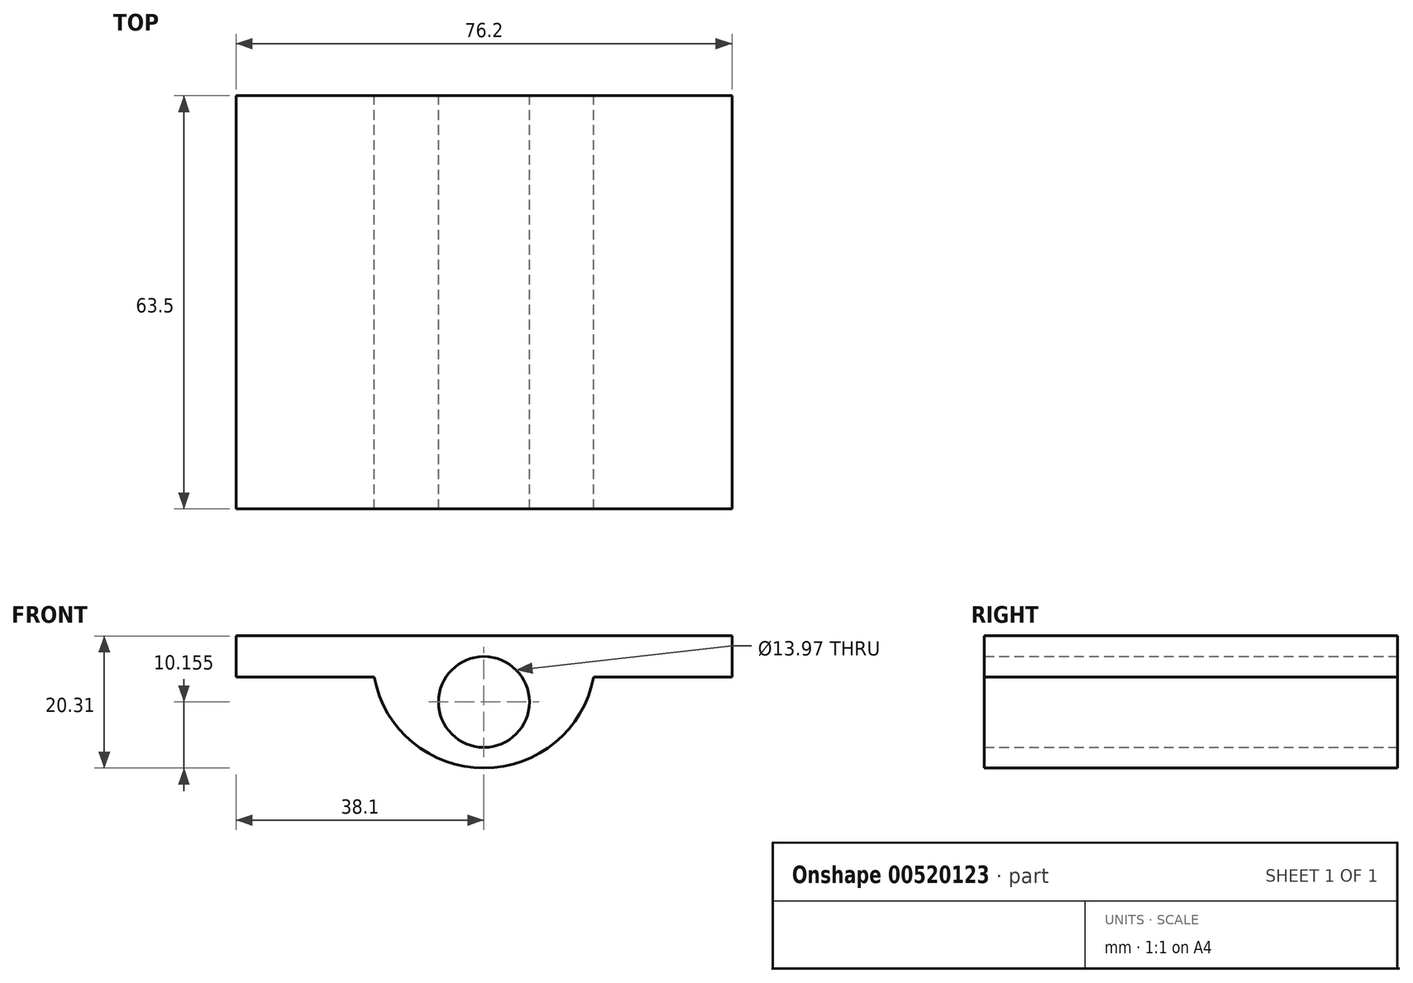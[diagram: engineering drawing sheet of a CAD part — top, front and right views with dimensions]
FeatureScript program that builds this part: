
annotation { "Feature Type Name" : "Feature", "Feature Type Description" : "" }
export const myFeature = defineFeature(function(context is Context, id is Id, definition is map)
    precondition{}
    {
        {
            var Q0;
            Q0=qCreatedBy(makeId("Front.planeOp"),FACE);
            var sketch = newSketch(context, id + "F0", { "sketchPlane" : qUnion([Q0])});
            skLineSegment(sketch, "E0.MirrorCS", {"start": v(38.1, 3.17) * mm, "end": v(38.1, -3.17) * mm});
            skLineSegment(sketch, "E1.MirrorCS", {"start": v(-38.1, 3.17) * mm, "end": v(-38.1, -3.17) * mm});
            skLineSegment(sketch, "E2.MirrorCS", {"start": v(38.1, -3.17) * mm, "end": v(16.85, -3.17) * mm});
            skLineSegment(sketch, "E3.MirrorCS", {"start": v(-38.1, -3.17) * mm, "end": v(-16.85, -3.17) * mm});
            skArc(sketch, "E4.MirrorCS", {"start": v(-16.85, -3.17) * mm, "mid": v(0, -17.14) * mm, "end": v(16.85, -3.18) * mm});
            skCircle(sketch, "E5", {"center": v(0, -6.99) * mm, "radius": 6.99 * mm});
            skLineSegment(sketch, "E6", {"start": v(0, 3.17) * mm, "end": v(38.1, 3.17) * mm});
            skLineSegment(sketch, "E7", {"start": v(0, 3.17) * mm, "end": v(-38.1, 3.17) * mm});
            skSolve(sketch);
        }
        {
            var Q0;
            Q0=makeQuery(id+"F0.imprint","IMPRINT",FACE,{"disambiguationData":[TD([[makeQuery(id+"F0.imprint","IMPRINT",EDGE,{"derivedFrom":sQuery(id+"F0.wireOp",EDGE,"E0.MirrorCS")}),-1.0]])]});
            extrude(context, id + "F1", {"entities" : qUnion([Q0]), "depth" : 63.5 * mm, "offsetDistance" : 25.4 * mm});
        }
    });
